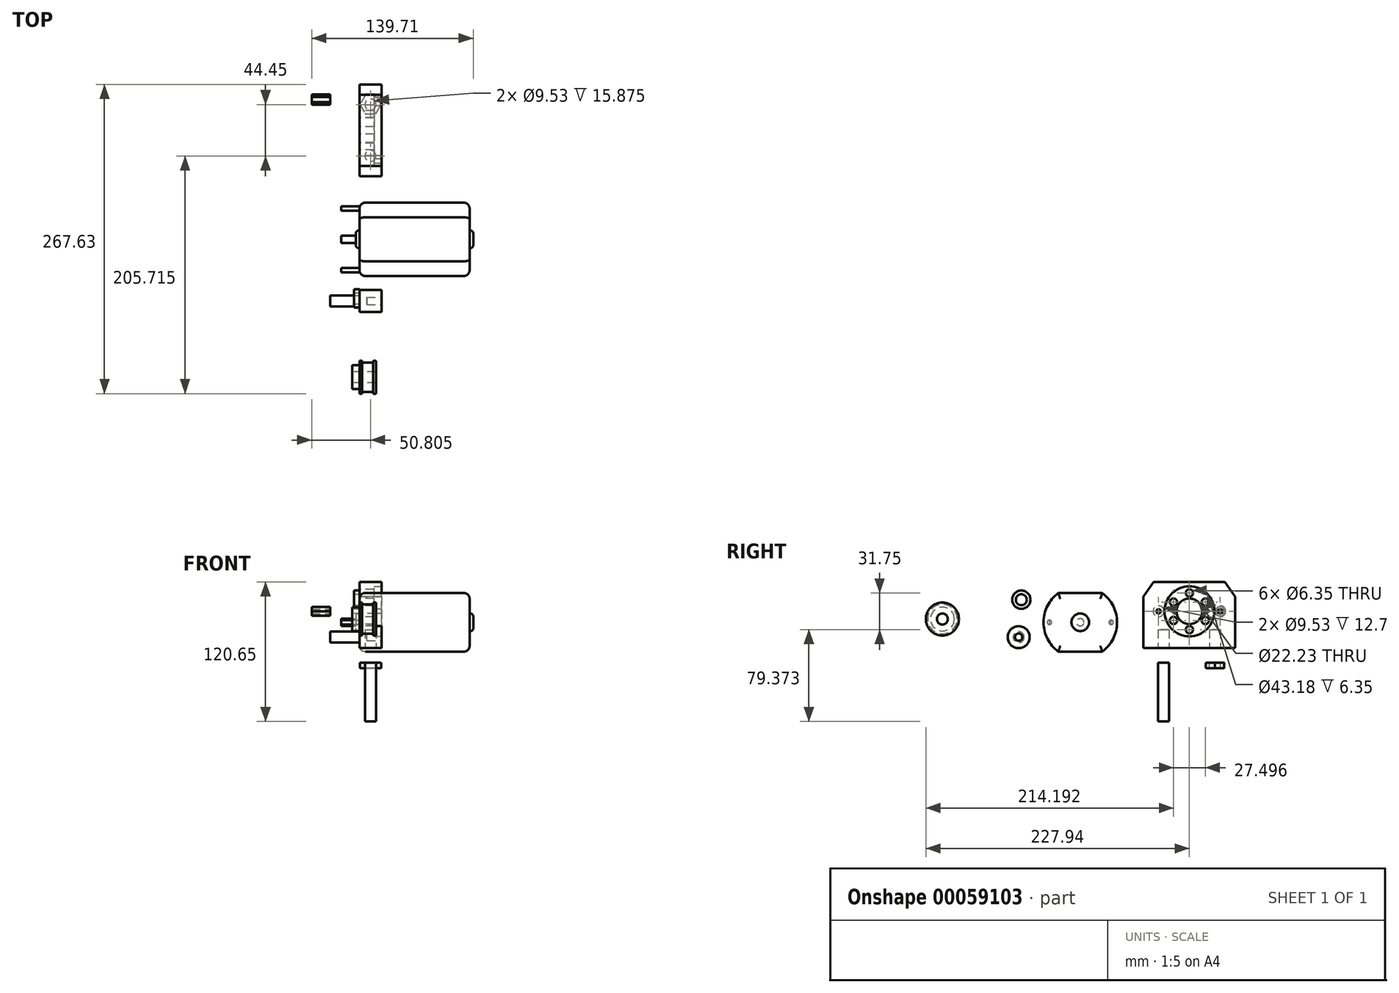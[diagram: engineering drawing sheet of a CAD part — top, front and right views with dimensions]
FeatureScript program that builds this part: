
annotation { "Feature Type Name" : "Feature", "Feature Type Description" : "" }
export const myFeature = defineFeature(function(context is Context, id is Id, definition is map)
    precondition{}
    {
        {
            var Q0;
            Q0=qCreatedBy(makeId("Right.planeOp"),FACE);
            var sketch = newSketch(context, id + "F0", { "sketchPlane" : qUnion([Q0])});
            skLineSegment(sketch, "E0.bottom", {"start": v(-22.45, 10.6) * mm, "end": v(15.65, 10.6) * mm});
            skLineSegment(sketch, "E0.top", {"start": v(-22.45, -40.2) * mm, "end": v(15.65, -40.2) * mm});
            skLineSegment(sketch, "E1", {"start": v(-22.45, 10.6) * mm, "end": v(-22.45, -40.2) * mm, "construction": true});
            skLineSegment(sketch, "E2", {"start": v(15.65, 10.6) * mm, "end": v(15.65, -40.2) * mm, "construction": true});
            skArc(sketch, "E3", {"start": v(-22.45, 10.6) * mm, "mid": v(-35.15, -14.8) * mm, "end": v(-22.45, -40.2) * mm});
            skArc(sketch, "E4", {"start": v(15.65, -40.2) * mm, "mid": v(28.35, -14.8) * mm, "end": v(15.65, 10.6) * mm});
            skSolve(sketch);
        }
        {
            var Q0;
            Q0=makeQuery(id+"F0.imprint","IMPRINT",FACE,{"disambiguationData":[TD([[makeQuery(id+"F0.imprint","IMPRINT",EDGE,{"derivedFrom":sQuery(id+"F0.wireOp",EDGE,"E0.bottom")}),-1.0]])]});
            extrude(context, id + "F1", {"entities" : qUnion([Q0]), "depth" : 95.25 * mm});
        }
        {
            var Q0;
            Q0=makeQuery(id+"F1.opExtrude","CAP_EDGE",EDGE,{"disambiguationData":[OSD([sQuery(id+"F0.wireOp",EDGE,"E3")])],"isStart":false});
            var Q1;
            Q1=makeQuery(id+"F1.opExtrude","CAP_EDGE",EDGE,{"disambiguationData":[OSD([sQuery(id+"F0.wireOp",EDGE,"E4")])],"isStart":false});
            var Q2;
            Q2=makeQuery(id+"F1.opExtrude","CAP_EDGE",EDGE,{"disambiguationData":[OSD([sQuery(id+"F0.wireOp",EDGE,"E0.bottom")])],"isStart":false});
            var Q3;
            Q3=makeQuery(id+"F1.opExtrude","CAP_EDGE",EDGE,{"disambiguationData":[OSD([sQuery(id+"F0.wireOp",EDGE,"E0.top")])],"isStart":false});
            fillet(context, id + "F2", {"entities" : qUnion([Q0, Q1, Q2, Q3]), "radius" : 5.08 * mm, "tangentPropagation" : true, "allowEdgeOverflow" : false});
        }
        {
            var Q0;
            Q0=makeQuery(id+"F1.opExtrude","CAP_EDGE",EDGE,{"disambiguationData":[OSD([sQuery(id+"F0.wireOp",EDGE,"E0.bottom")])],"isStart":true});
            var Q1;
            Q1=makeQuery(id+"F1.opExtrude","CAP_EDGE",EDGE,{"disambiguationData":[OSD([sQuery(id+"F0.wireOp",EDGE,"E0.top")])],"isStart":true});
            var Q2;
            Q2=makeQuery(id+"F1.opExtrude","CAP_EDGE",EDGE,{"disambiguationData":[OSD([sQuery(id+"F0.wireOp",EDGE,"E3")])],"isStart":true});
            var Q3;
            Q3=makeQuery(id+"F1.opExtrude","CAP_EDGE",EDGE,{"disambiguationData":[OSD([sQuery(id+"F0.wireOp",EDGE,"E4")])],"isStart":true});
            fillet(context, id + "F3", {"entities" : qUnion([Q0, Q1, Q2, Q3]), "radius" : 5.08 * mm, "tangentPropagation" : true, "allowEdgeOverflow" : false});
        }
        {
            var Q0;
            Q0=makeQuery(id+"F1.opExtrude","CAP_FACE",FACE,{"disambiguationData":[OSD([sQuery(id+"F0.wireOp",EDGE,"E0.bottom"),sQuery(id+"F0.wireOp",EDGE,"E0.top"),sQuery(id+"F0.wireOp",EDGE,"E3"),sQuery(id+"F0.wireOp",EDGE,"E4")])],"isStart":true});
            var sketch = newSketch(context, id + "F4", { "sketchPlane" : qUnion([Q0])});
            skLineSegment(sketch, "E5", {"start": v(-23.27, -14.8) * mm, "end": v(30.07, -14.8) * mm, "construction": true});
            skLineSegment(sketch, "E6", {"start": v(3.4, 5.53) * mm, "end": v(3.4, -35.11) * mm, "construction": true});
            skCircle(sketch, "E7", {"center": v(3.4, -14.8) * mm, "radius": 7.62 * mm});
            skSolve(sketch);
        }
        {
            var Q0;
            Q0=makeQuery(id+"F4.imprint","IMPRINT",FACE,{"disambiguationData":[TD([[makeQuery(id+"F4.imprint","IMPRINT",EDGE,{"derivedFrom":sQuery(id+"F4.wireOp",EDGE,"E7")}),1.0]])]});
            extrude(context, id + "F5", {"entities" : qUnion([Q0]), "operationType" : NewBodyOperationType.ADD, "depth" : 3.17 * mm});
        }
        {
            var Q0;
            Q0=makeQuery(id+"F5.opExtrude","CAP_FACE",FACE,{"disambiguationData":[OSD([sQuery(id+"F4.wireOp",EDGE,"E7")])],"isStart":false});
            var sketch = newSketch(context, id + "F6", { "sketchPlane" : qUnion([Q0])});
            skCircle(sketch, "E8", {"center": v(3.4, -14.8) * mm, "radius": 3.18 * mm});
            skSolve(sketch);
        }
        {
            var Q0;
            Q0=makeQuery(id+"F6.imprint","IMPRINT",FACE,{"disambiguationData":[TD([[makeQuery(id+"F6.imprint","IMPRINT",EDGE,{"derivedFrom":sQuery(id+"F6.wireOp",EDGE,"E8")}),1.0]])]});
            extrude(context, id + "F7", {"entities" : qUnion([Q0]), "operationType" : NewBodyOperationType.ADD, "depth" : 12.7 * mm});
        }
        {
            var Q0;
            Q0=makeQuery(id+"F5.opExtrude","CAP_EDGE",EDGE,{"disambiguationData":[OSD([sQuery(id+"F4.wireOp",EDGE,"E7")])],"isStart":false});
            fillet(context, id + "F8", {"entities" : qUnion([Q0]), "radius" : 2.54 * mm, "tangentPropagation" : true, "allowEdgeOverflow" : false});
        }
        {
            var Q0;
            Q0=makeQuery(id+"F1.opExtrude","CAP_FACE",FACE,{"disambiguationData":[OSD([sQuery(id+"F0.wireOp",EDGE,"E0.bottom"),sQuery(id+"F0.wireOp",EDGE,"E0.top"),sQuery(id+"F0.wireOp",EDGE,"E3"),sQuery(id+"F0.wireOp",EDGE,"E4")])],"isStart":false});
            var sketch = newSketch(context, id + "F9", { "sketchPlane" : qUnion([Q0])});
            skLineSegment(sketch, "E9", {"start": v(-30.07, -14.8) * mm, "end": v(23.27, -14.8) * mm, "construction": true});
            skLineSegment(sketch, "E10", {"start": v(-3.4, 5.53) * mm, "end": v(-3.4, -35.11) * mm, "construction": true});
            skCircle(sketch, "E11", {"center": v(-3.4, -14.8) * mm, "radius": 7.62 * mm});
            skSolve(sketch);
        }
        {
            var Q0;
            Q0=makeQuery(id+"F9.imprint","IMPRINT",FACE,{"disambiguationData":[TD([[makeQuery(id+"F9.imprint","IMPRINT",EDGE,{"derivedFrom":sQuery(id+"F9.wireOp",EDGE,"E11")}),1.0]])]});
            extrude(context, id + "F10", {"entities" : qUnion([Q0]), "operationType" : NewBodyOperationType.ADD, "depth" : 3.17 * mm});
        }
        {
            var Q0;
            Q0=makeQuery(id+"F10.opExtrude","CAP_EDGE",EDGE,{"disambiguationData":[OSD([sQuery(id+"F9.wireOp",EDGE,"E11")])],"isStart":false});
            fillet(context, id + "F11", {"entities" : qUnion([Q0]), "radius" : 2.54 * mm, "tangentPropagation" : true, "allowEdgeOverflow" : false});
        }
        {
            var Q0;
            Q0=makeQuery(id+"F1.opExtrude","CAP_FACE",FACE,{"disambiguationData":[OSD([sQuery(id+"F0.wireOp",EDGE,"E0.bottom"),sQuery(id+"F0.wireOp",EDGE,"E0.top"),sQuery(id+"F0.wireOp",EDGE,"E3"),sQuery(id+"F0.wireOp",EDGE,"E4")])],"isStart":true});
            var sketch = newSketch(context, id + "F12", { "sketchPlane" : qUnion([Q0])});
            skLineSegment(sketch, "E12", {"start": v(-23.27, -14.8) * mm, "end": v(30.07, -14.8) * mm, "construction": true});
            skCircle(sketch, "E13", {"center": v(-23.27, -14.8) * mm, "radius": 1.9 * mm});
            skCircle(sketch, "E14", {"center": v(30.07, -14.8) * mm, "radius": 1.9 * mm});
            skSolve(sketch);
        }
        {
            var Q0;
            {var subQ0=sQuery(id+"F12.wireOp",EDGE,"E13");var subQ1=sQuery(id+"F0.wireOp",EDGE,"E4");var subQ2=makeQuery(id+"F3.opFillet","BLEND_EDGE",EDGE,{"blendedFrom":[makeQuery(id+"F1.opExtrude","CAP_EDGE",EDGE,{"disambiguationData":[OSD([subQ1])],"isStart":true}),makeQuery(id+"F1.opExtrude","CAP_FACE",FACE,{"disambiguationData":[OSD([sQuery(id+"F0.wireOp",EDGE,"E0.bottom"),sQuery(id+"F0.wireOp",EDGE,"E0.top"),sQuery(id+"F0.wireOp",EDGE,"E3"),subQ1])],"isStart":true})],"blendedInto":[makeQuery(id+"F1.opExtrude","CAP_FACE",FACE,{"disambiguationData":[OSD([sQuery(id+"F0.wireOp",EDGE,"E0.bottom"),sQuery(id+"F0.wireOp",EDGE,"E0.top"),sQuery(id+"F0.wireOp",EDGE,"E3"),subQ1])],"isStart":true})]});var subQ3=makeQuery(id+"F12.imprint","INTERSECT",VERTEX,{"disambiguationData":[OD(0.0)],"derivedFrom":[subQ2,subQ0]});Q0=makeQuery(id+"F12.imprint","IMPRINT",FACE,{"disambiguationData":[TD([[makeQuery(id+"F12.imprint","IMPRINT",EDGE,{"disambiguationData":[TD([[subQ3,1.0]])],"derivedFrom":subQ0}),1.0]])]});}
            var Q1;
            {var subQ0=sQuery(id+"F12.wireOp",EDGE,"E13");var subQ1=sQuery(id+"F0.wireOp",EDGE,"E4");var subQ2=makeQuery(id+"F3.opFillet","BLEND_EDGE",EDGE,{"blendedFrom":[makeQuery(id+"F1.opExtrude","CAP_EDGE",EDGE,{"disambiguationData":[OSD([subQ1])],"isStart":true}),makeQuery(id+"F1.opExtrude","CAP_FACE",FACE,{"disambiguationData":[OSD([sQuery(id+"F0.wireOp",EDGE,"E0.bottom"),sQuery(id+"F0.wireOp",EDGE,"E0.top"),sQuery(id+"F0.wireOp",EDGE,"E3"),subQ1])],"isStart":true})],"blendedInto":[makeQuery(id+"F1.opExtrude","CAP_FACE",FACE,{"disambiguationData":[OSD([sQuery(id+"F0.wireOp",EDGE,"E0.bottom"),sQuery(id+"F0.wireOp",EDGE,"E0.top"),sQuery(id+"F0.wireOp",EDGE,"E3"),subQ1])],"isStart":true})]});var subQ3=makeQuery(id+"F12.imprint","INTERSECT",VERTEX,{"disambiguationData":[OD(0.0)],"derivedFrom":[subQ2,subQ0]});Q1=makeQuery(id+"F12.imprint","IMPRINT",FACE,{"disambiguationData":[TD([[makeQuery(id+"F12.imprint","IMPRINT",EDGE,{"disambiguationData":[TD([[subQ3,-1.0]])],"derivedFrom":subQ0}),1.0]])]});}
            var Q2;
            {var subQ0=sQuery(id+"F12.wireOp",EDGE,"E14");var subQ1=sQuery(id+"F0.wireOp",EDGE,"E3");var subQ2=makeQuery(id+"F3.opFillet","BLEND_EDGE",EDGE,{"blendedFrom":[makeQuery(id+"F1.opExtrude","CAP_EDGE",EDGE,{"disambiguationData":[OSD([subQ1])],"isStart":true}),makeQuery(id+"F1.opExtrude","CAP_FACE",FACE,{"disambiguationData":[OSD([sQuery(id+"F0.wireOp",EDGE,"E0.bottom"),sQuery(id+"F0.wireOp",EDGE,"E0.top"),subQ1,sQuery(id+"F0.wireOp",EDGE,"E4")])],"isStart":true})],"blendedInto":[makeQuery(id+"F1.opExtrude","CAP_FACE",FACE,{"disambiguationData":[OSD([sQuery(id+"F0.wireOp",EDGE,"E0.bottom"),sQuery(id+"F0.wireOp",EDGE,"E0.top"),subQ1,sQuery(id+"F0.wireOp",EDGE,"E4")])],"isStart":true})]});var subQ3=makeQuery(id+"F12.imprint","INTERSECT",VERTEX,{"disambiguationData":[OD(0.0)],"derivedFrom":[subQ2,subQ0]});Q2=makeQuery(id+"F12.imprint","IMPRINT",FACE,{"disambiguationData":[TD([[makeQuery(id+"F12.imprint","IMPRINT",EDGE,{"disambiguationData":[TD([[subQ3,-1.0]])],"derivedFrom":subQ0}),1.0]])]});}
            var Q3;
            {var subQ0=sQuery(id+"F12.wireOp",EDGE,"E14");var subQ1=sQuery(id+"F0.wireOp",EDGE,"E3");var subQ2=makeQuery(id+"F3.opFillet","BLEND_EDGE",EDGE,{"blendedFrom":[makeQuery(id+"F1.opExtrude","CAP_EDGE",EDGE,{"disambiguationData":[OSD([subQ1])],"isStart":true}),makeQuery(id+"F1.opExtrude","CAP_FACE",FACE,{"disambiguationData":[OSD([sQuery(id+"F0.wireOp",EDGE,"E0.bottom"),sQuery(id+"F0.wireOp",EDGE,"E0.top"),subQ1,sQuery(id+"F0.wireOp",EDGE,"E4")])],"isStart":true})],"blendedInto":[makeQuery(id+"F1.opExtrude","CAP_FACE",FACE,{"disambiguationData":[OSD([sQuery(id+"F0.wireOp",EDGE,"E0.bottom"),sQuery(id+"F0.wireOp",EDGE,"E0.top"),subQ1,sQuery(id+"F0.wireOp",EDGE,"E4")])],"isStart":true})]});var subQ3=makeQuery(id+"F12.imprint","INTERSECT",VERTEX,{"disambiguationData":[OD(0.0)],"derivedFrom":[subQ2,subQ0]});Q3=makeQuery(id+"F12.imprint","IMPRINT",FACE,{"disambiguationData":[TD([[makeQuery(id+"F12.imprint","IMPRINT",EDGE,{"disambiguationData":[TD([[subQ3,1.0]])],"derivedFrom":subQ0}),1.0]])]});}
            extrude(context, id + "F13", {"entities" : qUnion([Q0, Q1, Q2, Q3]), "operationType" : NewBodyOperationType.ADD, "depth" : 15.88 * mm});
        }
        {
            var Q0;
            Q0=qCreatedBy(makeId("Right.planeOp"),FACE);
            var sketch = newSketch(context, id + "F14", { "sketchPlane" : qUnion([Q0])});
            skLineSegment(sketch, "E15.bottom", {"start": v(130.66, 20.15) * mm, "end": v(51.28, 20.15) * mm});
            skLineSegment(sketch, "E15.top", {"start": v(130.66, -37) * mm, "end": v(51.28, -37) * mm});
            skLineSegment(sketch, "E15.left", {"start": v(130.66, 20.15) * mm, "end": v(130.66, -37) * mm});
            skLineSegment(sketch, "E15.right", {"start": v(51.28, 20.15) * mm, "end": v(51.28, -37) * mm});
            skLineSegment(sketch, "E16", {"start": v(117.64, 20.15) * mm, "end": v(117.64, -37) * mm, "construction": true});
            skLineSegment(sketch, "E17", {"start": v(64.3, 20.15) * mm, "end": v(64.3, -37) * mm, "construction": true});
            skLineSegment(sketch, "E18", {"start": v(130.66, -5.25) * mm, "end": v(51.28, -5.25) * mm, "construction": true});
            skCircle(sketch, "E19", {"center": v(117.64, -5.25) * mm, "radius": 1.9 * mm});
            skCircle(sketch, "E20", {"center": v(64.3, -5.25) * mm, "radius": 1.9 * mm});
            skLineSegment(sketch, "E21", {"start": v(90.97, 20.15) * mm, "end": v(90.97, -37) * mm, "construction": true});
            skSolve(sketch);
        }
        {
            var Q0;
            Q0=makeQuery(id+"F14.imprint","IMPRINT",FACE,{"disambiguationData":[TD([[makeQuery(id+"F14.imprint","IMPRINT",EDGE,{"derivedFrom":sQuery(id+"F14.wireOp",EDGE,"E15.bottom")}),1.0]])]});
            extrude(context, id + "F15", {"entities" : qUnion([Q0]), "depth" : 19.05 * mm});
        }
        {
            var Q0;
            Q0=makeQuery(id+"F15.opExtrude","CAP_FACE",FACE,{"disambiguationData":[OSD([sQuery(id+"F14.wireOp",EDGE,"E15.bottom"),sQuery(id+"F14.wireOp",EDGE,"E15.top"),sQuery(id+"F14.wireOp",EDGE,"E15.left"),sQuery(id+"F14.wireOp",EDGE,"E15.right"),sQuery(id+"F14.wireOp",EDGE,"E19"),sQuery(id+"F14.wireOp",EDGE,"E20")])],"isStart":true});
            var sketch = newSketch(context, id + "F16", { "sketchPlane" : qUnion([Q0])});
            skCircle(sketch, "E22", {"center": v(-117.64, -5.25) * mm, "radius": 4.76 * mm});
            skCircle(sketch, "E23", {"center": v(-64.3, -5.25) * mm, "radius": 4.76 * mm});
            skSolve(sketch);
        }
        {
            var Q0;
            Q0=makeQuery(id+"F16.imprint","IMPRINT",FACE,{"disambiguationData":[TD([[makeQuery(id+"F16.imprint","IMPRINT",EDGE,{"derivedFrom":sQuery(id+"F16.wireOp",EDGE,"E22")}),1.0]])]});
            var Q1;
            Q1=makeQuery(id+"F16.imprint","IMPRINT",FACE,{"disambiguationData":[TD([[makeQuery(id+"F16.imprint","IMPRINT",EDGE,{"derivedFrom":sQuery(id+"F16.wireOp",EDGE,"E23")}),1.0]])]});
            extrude(context, id + "F17", {"entities" : qUnion([Q0, Q1]), "operationType" : NewBodyOperationType.REMOVE, "oppositeDirection" : true, "depth" : 12.7 * mm});
        }
        {
            var Q0;
            Q0=makeQuery(id+"F15.opExtrude","CAP_FACE",FACE,{"disambiguationData":[OSD([sQuery(id+"F14.wireOp",EDGE,"E15.bottom"),sQuery(id+"F14.wireOp",EDGE,"E15.top"),sQuery(id+"F14.wireOp",EDGE,"E15.left"),sQuery(id+"F14.wireOp",EDGE,"E15.right"),sQuery(id+"F14.wireOp",EDGE,"E19"),sQuery(id+"F14.wireOp",EDGE,"E20")])],"isStart":true});
            var sketch = newSketch(context, id + "F18", { "sketchPlane" : qUnion([Q0])});
            skLineSegment(sketch, "E24", {"start": v(-90.97, 20.15) * mm, "end": v(-90.97, -37) * mm, "construction": true});
            skLineSegment(sketch, "E25", {"start": v(-117.64, -5.25) * mm, "end": v(-64.3, -5.25) * mm, "construction": true});
            skCircle(sketch, "E26", {"center": v(-90.97, -5.25) * mm, "radius": 11.11 * mm});
            skPoint(sketch, "E26.centerSnap1", {"position": v(-90.97, -5.25) * mm});
            skSolve(sketch);
        }
        {
            var Q0;
            Q0=makeQuery(id+"F18.imprint","IMPRINT",FACE,{"disambiguationData":[TD([[makeQuery(id+"F18.imprint","IMPRINT",EDGE,{"derivedFrom":sQuery(id+"F18.wireOp",EDGE,"E26")}),1.0]])]});
            extrude(context, id + "F19", {"entities" : qUnion([Q0]), "operationType" : NewBodyOperationType.REMOVE, "endBound" : BoundingType.THROUGH_ALL, "oppositeDirection" : true, "depth" : 25.4 * mm});
        }
        {
            var Q0;
            Q0=makeQuery(id+"F15.opExtrude","SWEPT_EDGE",EDGE,{"disambiguationData":[OSD([sQuery(id+"F14.wireOp",EDGE,"E15.bottom"),sQuery(id+"F14.wireOp",EDGE,"E15.left")])]});
            var Q1;
            Q1=makeQuery(id+"F15.opExtrude","SWEPT_EDGE",EDGE,{"disambiguationData":[OSD([sQuery(id+"F14.wireOp",EDGE,"E15.bottom"),sQuery(id+"F14.wireOp",EDGE,"E15.right")])]});
            chamfer(context, id + "F20", {"entities" : qUnion([Q0, Q1]), "chamferType" : ChamferType.TWO_OFFSETS, "width1" : 8.9 * mm, "oppositeDirection" : false, "width2" : 12.7 * mm, "tangentPropagation" : true});
        }
        {
            var Q0;
            Q0=makeQuery(id+"F15.opExtrude","SWEPT_FACE",FACE,{"disambiguationData":[OSD([sQuery(id+"F14.wireOp",EDGE,"E15.top")])]});
            var sketch = newSketch(context, id + "F21", { "sketchPlane" : qUnion([Q0])});
            skLineSegment(sketch, "E27", {"start": v(9.53, -51.28) * mm, "end": v(9.53, -130.66) * mm, "construction": true});
            skLineSegment(sketch, "E28", {"start": v(0, -68.74) * mm, "end": v(19.05, -68.74) * mm, "construction": true});
            skLineSegment(sketch, "E29", {"start": v(0, -113.2) * mm, "end": v(19.05, -113.2) * mm, "construction": true});
            skCircle(sketch, "E30", {"center": v(9.53, -68.74) * mm, "radius": 4.76 * mm});
            skCircle(sketch, "E31", {"center": v(9.53, -113.2) * mm, "radius": 4.76 * mm});
            skLineSegment(sketch, "E32.0", {"start": v(19.05, -51.28) * mm, "end": v(0, -51.28) * mm, "construction": true});
            skLineSegment(sketch, "E33.0", {"start": v(19.05, -130.66) * mm, "end": v(0, -130.66) * mm, "construction": true});
            skLineSegment(sketch, "E34", {"start": v(0, -90.97) * mm, "end": v(19.05, -90.97) * mm, "construction": true});
            skSolve(sketch);
        }
        {
            var Q0;
            Q0=makeQuery(id+"F21.imprint","IMPRINT",FACE,{"disambiguationData":[TD([[makeQuery(id+"F21.imprint","IMPRINT",EDGE,{"derivedFrom":sQuery(id+"F21.wireOp",EDGE,"E30")}),1.0]])]});
            var Q1;
            Q1=makeQuery(id+"F21.imprint","IMPRINT",FACE,{"disambiguationData":[TD([[makeQuery(id+"F21.imprint","IMPRINT",EDGE,{"derivedFrom":sQuery(id+"F21.wireOp",EDGE,"E31")}),1.0]])]});
            extrude(context, id + "F22", {"entities" : qUnion([Q0, Q1]), "operationType" : NewBodyOperationType.REMOVE, "oppositeDirection" : true, "depth" : 15.88 * mm});
        }
        {
            var Q0;
            Q0=makeQuery(id+"F15.opExtrude","CAP_FACE",FACE,{"disambiguationData":[OSD([sQuery(id+"F14.wireOp",EDGE,"E15.bottom"),sQuery(id+"F14.wireOp",EDGE,"E15.top"),sQuery(id+"F14.wireOp",EDGE,"E15.left"),sQuery(id+"F14.wireOp",EDGE,"E15.right"),sQuery(id+"F14.wireOp",EDGE,"E19"),sQuery(id+"F14.wireOp",EDGE,"E20")])],"isStart":true});
            var sketch = newSketch(context, id + "F23", { "sketchPlane" : qUnion([Q0])});
            skCircle(sketch, "E35", {"center": v(-90.97, 10.62) * mm, "radius": 3.18 * mm});
            skCircle(sketch, "E36.1.0", {"center": v(-104.72, 2.69) * mm, "radius": 3.18 * mm});
            skCircle(sketch, "E36.2.0", {"center": v(-104.72, -13.19) * mm, "radius": 3.18 * mm});
            skCircle(sketch, "E36.3.0", {"center": v(-90.97, -21.13) * mm, "radius": 3.18 * mm});
            skCircle(sketch, "E36.4.0", {"center": v(-77.22, -13.19) * mm, "radius": 3.18 * mm});
            skCircle(sketch, "E36.5.0", {"center": v(-77.22, 2.69) * mm, "radius": 3.18 * mm});
            skPoint(sketch, "E36.center", {"position": v(-90.97, -5.25) * mm});
            skPoint(sketch, "E37.orphan", {"position": v(-90.97, 20.15) * mm});
            skLineSegment(sketch, "E38", {"start": v(-90.97, 20.15) * mm, "end": v(-90.97, -37) * mm, "construction": true});
            skLineSegment(sketch, "E39", {"start": v(-90.97, -37) * mm, "end": v(-92.08, -36.2) * mm, "construction": true});
            skSolve(sketch);
        }
        {
            var Q0;
            Q0=makeQuery(id+"F23.imprint","IMPRINT",FACE,{"disambiguationData":[TD([[makeQuery(id+"F23.imprint","IMPRINT",EDGE,{"derivedFrom":sQuery(id+"F23.wireOp",EDGE,"E35")}),1.0]])]});
            var Q1;
            Q1=makeQuery(id+"F23.imprint","IMPRINT",FACE,{"disambiguationData":[TD([[makeQuery(id+"F23.imprint","IMPRINT",EDGE,{"derivedFrom":sQuery(id+"F23.wireOp",EDGE,"E36.5.0")}),1.0]])]});
            var Q2;
            Q2=makeQuery(id+"F23.imprint","IMPRINT",FACE,{"disambiguationData":[TD([[makeQuery(id+"F23.imprint","IMPRINT",EDGE,{"derivedFrom":sQuery(id+"F23.wireOp",EDGE,"E36.4.0")}),1.0]])]});
            var Q3;
            Q3=makeQuery(id+"F23.imprint","IMPRINT",FACE,{"disambiguationData":[TD([[makeQuery(id+"F23.imprint","IMPRINT",EDGE,{"derivedFrom":sQuery(id+"F23.wireOp",EDGE,"E36.3.0")}),1.0]])]});
            var Q4;
            Q4=makeQuery(id+"F23.imprint","IMPRINT",FACE,{"disambiguationData":[TD([[makeQuery(id+"F23.imprint","IMPRINT",EDGE,{"derivedFrom":sQuery(id+"F23.wireOp",EDGE,"E36.2.0")}),1.0]])]});
            var Q5;
            Q5=makeQuery(id+"F23.imprint","IMPRINT",FACE,{"disambiguationData":[TD([[makeQuery(id+"F23.imprint","IMPRINT",EDGE,{"derivedFrom":sQuery(id+"F23.wireOp",EDGE,"E36.1.0")}),1.0]])]});
            extrude(context, id + "F24", {"entities" : qUnion([Q0, Q1, Q2, Q3, Q4, Q5]), "operationType" : NewBodyOperationType.REMOVE, "endBound" : BoundingType.THROUGH_ALL, "oppositeDirection" : true, "depth" : 25.4 * mm});
        }
        {
            var Q0;
            Q0=makeQuery(id+"F15.opExtrude","CAP_FACE",FACE,{"disambiguationData":[OSD([sQuery(id+"F14.wireOp",EDGE,"E15.bottom"),sQuery(id+"F14.wireOp",EDGE,"E15.top"),sQuery(id+"F14.wireOp",EDGE,"E15.left"),sQuery(id+"F14.wireOp",EDGE,"E15.right"),sQuery(id+"F14.wireOp",EDGE,"E19"),sQuery(id+"F14.wireOp",EDGE,"E20")])],"isStart":false});
            var sketch = newSketch(context, id + "F25", { "sketchPlane" : qUnion([Q0])});
            skCircle(sketch, "E40.0", {"center": v(90.97, -5.25) * mm, "radius": 11.11 * mm});
            skCircle(sketch, "E41", {"center": v(90.97, -5.25) * mm, "radius": 21.59 * mm});
            skSolve(sketch);
        }
        {
            var Q0;
            Q0=makeQuery(id+"F25.imprint","IMPRINT",FACE,{"disambiguationData":[TD([[makeQuery(id+"F25.imprint","IMPRINT",EDGE,{"derivedFrom":sQuery(id+"F25.wireOp",EDGE,"E40.0")}),-1.0]])]});
            extrude(context, id + "F26", {"entities" : qUnion([Q0]), "operationType" : NewBodyOperationType.REMOVE, "oppositeDirection" : true, "depth" : 6.35 * mm});
        }
        {
            var Q0;
            Q0=qCreatedBy(makeId("Right.planeOp"),FACE);
            var sketch = newSketch(context, id + "F27", { "sketchPlane" : qUnion([Q0])});
            skCircle(sketch, "E42", {"center": v(-56.7, -27.63) * mm, "radius": 9.53 * mm});
            skSolve(sketch);
        }
        {
            var Q0;
            Q0=makeQuery(id+"F27.imprint","IMPRINT",FACE,{"disambiguationData":[TD([[makeQuery(id+"F27.imprint","IMPRINT",EDGE,{"derivedFrom":sQuery(id+"F27.wireOp",EDGE,"E42")}),1.0]])]});
            extrude(context, id + "F28", {"entities" : qUnion([Q0]), "depth" : 19.05 * mm});
        }
        {
            var Q0;
            Q0=makeQuery(id+"F28.opExtrude","CAP_FACE",FACE,{"disambiguationData":[OSD([sQuery(id+"F27.wireOp",EDGE,"E42")])],"isStart":true});
            var sketch = newSketch(context, id + "F29", { "sketchPlane" : qUnion([Q0])});
            skCircle(sketch, "E43", {"center": v(56.7, -27.63) * mm, "radius": 4.76 * mm});
            skSolve(sketch);
        }
        {
            var Q0;
            Q0=makeQuery(id+"F29.imprint","IMPRINT",FACE,{"disambiguationData":[TD([[makeQuery(id+"F29.imprint","IMPRINT",EDGE,{"derivedFrom":sQuery(id+"F29.wireOp",EDGE,"E43")}),1.0]])]});
            extrude(context, id + "F30", {"entities" : qUnion([Q0]), "operationType" : NewBodyOperationType.ADD, "depth" : 25.4 * mm});
        }
        {
            var Q0;
            Q0=makeQuery(id+"F28.opExtrude","CAP_FACE",FACE,{"disambiguationData":[OSD([sQuery(id+"F27.wireOp",EDGE,"E42")])],"isStart":false});
            var sketch = newSketch(context, id + "F31", { "sketchPlane" : qUnion([Q0])});
            skCircle(sketch, "E44", {"center": v(-56.7, -27.63) * mm, "radius": 3.17 * mm});
            skSolve(sketch);
        }
        {
            var Q0;
            Q0=makeQuery(id+"F31.imprint","IMPRINT",FACE,{"disambiguationData":[TD([[makeQuery(id+"F31.imprint","IMPRINT",EDGE,{"derivedFrom":sQuery(id+"F31.wireOp",EDGE,"E44")}),1.0]])]});
            extrude(context, id + "F32", {"entities" : qUnion([Q0]), "operationType" : NewBodyOperationType.REMOVE, "oppositeDirection" : true, "depth" : 12.7 * mm});
        }
        {
            var Q0;
            Q0=qCreatedBy(makeId("Right.planeOp"),FACE);
            var sketch = newSketch(context, id + "F33", { "sketchPlane" : qUnion([Q0])});
            skCircle(sketch, "E45", {"center": v(-122.68, -11.96) * mm, "radius": 14.29 * mm});
            skCircle(sketch, "E46", {"center": v(-122.68, -11.96) * mm, "radius": 4.76 * mm});
            skSolve(sketch);
        }
        {
            var Q0;
            Q0=makeQuery(id+"F33.imprint","IMPRINT",FACE,{"disambiguationData":[TD([[makeQuery(id+"F33.imprint","IMPRINT",EDGE,{"derivedFrom":sQuery(id+"F33.wireOp",EDGE,"E45")}),1.0]])]});
            extrude(context, id + "F34", {"entities" : qUnion([Q0]), "depth" : 2.4 * mm});
        }
        {
            var Q0;
            Q0=makeQuery(id+"F34.opExtrude","CAP_FACE",FACE,{"disambiguationData":[OSD([sQuery(id+"F33.wireOp",EDGE,"E45"),sQuery(id+"F33.wireOp",EDGE,"E46")])],"isStart":true});
            var sketch = newSketch(context, id + "F35", { "sketchPlane" : qUnion([Q0])});
            skCircle(sketch, "E47", {"center": v(122.68, -11.96) * mm, "radius": 10.31 * mm});
            skSolve(sketch);
        }
        {
            var Q0;
            Q0=makeQuery(id+"F35.imprint","IMPRINT",FACE,{"disambiguationData":[TD([[makeQuery(id+"F35.imprint","IMPRINT",EDGE,{"derivedFrom":sQuery(id+"F35.wireOp",EDGE,"E47")}),1.0]])]});
            extrude(context, id + "F36", {"entities" : qUnion([Q0]), "operationType" : NewBodyOperationType.ADD, "depth" : 6.35 * mm});
        }
        {
            var Q0;
            Q0=makeQuery(id+"F34.opExtrude","CAP_FACE",FACE,{"disambiguationData":[OSD([sQuery(id+"F33.wireOp",EDGE,"E45"),sQuery(id+"F33.wireOp",EDGE,"E46")])],"isStart":false});
            var sketch = newSketch(context, id + "F37", { "sketchPlane" : qUnion([Q0])});
            skCircle(sketch, "E48", {"center": v(-122.68, -11.96) * mm, "radius": 12.7 * mm});
            skCircle(sketch, "E49", {"center": v(-122.68, -11.96) * mm, "radius": 4.76 * mm});
            skSolve(sketch);
        }
        {
            var Q0;
            Q0=makeQuery(id+"F37.imprint","IMPRINT",FACE,{"disambiguationData":[TD([[makeQuery(id+"F37.imprint","IMPRINT",EDGE,{"derivedFrom":sQuery(id+"F37.wireOp",EDGE,"E48")}),1.0]])]});
            extrude(context, id + "F38", {"entities" : qUnion([Q0]), "operationType" : NewBodyOperationType.ADD, "depth" : 11.9 * mm});
        }
        {
            var Q0;
            Q0=makeQuery(id+"F38.opExtrude","CAP_FACE",FACE,{"disambiguationData":[OSD([sQuery(id+"F37.wireOp",EDGE,"E48"),sQuery(id+"F37.wireOp",EDGE,"E49")])],"isStart":false});
            var sketch = newSketch(context, id + "F39", { "sketchPlane" : qUnion([Q0])});
            skCircle(sketch, "E50", {"center": v(-122.68, -11.96) * mm, "radius": 4.76 * mm});
            skCircle(sketch, "E51", {"center": v(-122.68, -11.96) * mm, "radius": 14.29 * mm});
            skSolve(sketch);
        }
        {
            var Q0;
            Q0=makeQuery(id+"F39.imprint","IMPRINT",FACE,{"disambiguationData":[TD([[makeQuery(id+"F39.imprint","IMPRINT",EDGE,{"derivedFrom":sQuery(id+"F39.wireOp",EDGE,"E51")}),1.0]])]});
            extrude(context, id + "F40", {"entities" : qUnion([Q0]), "operationType" : NewBodyOperationType.ADD, "oppositeDirection" : true, "depth" : 2.4 * mm});
        }
        {
            var Q0;
            Q0=qCreatedBy(makeId("Right.planeOp"),FACE);
            var sketch = newSketch(context, id + "F41", { "sketchPlane" : qUnion([Q0])});
            skCircle(sketch, "E52", {"center": v(-54.42, 4.77) * mm, "radius": 7.94 * mm});
            skCircle(sketch, "E53", {"center": v(-54.42, 4.77) * mm, "radius": 4.76 * mm});
            skSolve(sketch);
        }
        {
            var Q0;
            Q0=makeQuery(id+"F41.imprint","IMPRINT",FACE,{"disambiguationData":[TD([[makeQuery(id+"F41.imprint","IMPRINT",EDGE,{"derivedFrom":sQuery(id+"F41.wireOp",EDGE,"E52")}),1.0]])]});
            extrude(context, id + "F42", {"entities" : qUnion([Q0]), "oppositeDirection" : true, "depth" : 4.75 * mm});
        }
        {
            var Q0;
            Q0=makeQuery(id+"F15.opExtrude","CAP_FACE",FACE,{"disambiguationData":[OSD([sQuery(id+"F14.wireOp",EDGE,"E15.bottom"),sQuery(id+"F14.wireOp",EDGE,"E15.top"),sQuery(id+"F14.wireOp",EDGE,"E15.left"),sQuery(id+"F14.wireOp",EDGE,"E15.right"),sQuery(id+"F14.wireOp",EDGE,"E19"),sQuery(id+"F14.wireOp",EDGE,"E20")])],"isStart":true});
            cPlane(context, id + "F43", {"entities" : qUnion([Q0]), "cplaneType" : CPlaneType.OFFSET, "offset" : 25.4 * mm, "width" : 152.4 * mm, "height" : 152.4 * mm});
        }
        {
            var Q0;
            Q0=qCreatedBy(id+"F43.planeOp",FACE);
            var sketch = newSketch(context, id + "F44", { "sketchPlane" : qUnion([Q0])});
            skCircle(sketch, "E54.0", {"center": v(-117.64, -5.25) * mm, "radius": 1.9 * mm, "construction": true});
            skCircle(sketch, "E55.0", {"center": v(-117.64, -5.25) * mm, "radius": 4.76 * mm, "construction": true});
            skCircle(sketch, "E56.cCircle", {"center": v(-117.64, -5.25) * mm, "radius": 3.8 * mm, "construction": true});
            skLineSegment(sketch, "E56.0", {"start": v(-113.24, -5.25) * mm, "end": v(-115.44, -9.06) * mm});
            skLineSegment(sketch, "E56.1", {"start": v(-115.44, -9.06) * mm, "end": v(-119.84, -9.06) * mm});
            skLineSegment(sketch, "E56.2", {"start": v(-119.84, -9.06) * mm, "end": v(-122.04, -5.25) * mm});
            skLineSegment(sketch, "E56.3", {"start": v(-122.04, -5.25) * mm, "end": v(-119.84, -1.44) * mm});
            skLineSegment(sketch, "E56.4", {"start": v(-119.84, -1.44) * mm, "end": v(-115.44, -1.44) * mm});
            skLineSegment(sketch, "E56.5", {"start": v(-115.44, -1.44) * mm, "end": v(-113.24, -5.25) * mm});
            skPoint(sketch, "E56.0.midPoint", {"position": v(-114.34, -7.16) * mm});
            skCircle(sketch, "E57", {"center": v(-117.64, -5.25) * mm, "radius": 1.9 * mm});
            skSolve(sketch);
        }
        {
            var Q0;
            Q0=makeQuery(id+"F44.imprint","IMPRINT",FACE,{"disambiguationData":[TD([[makeQuery(id+"F44.imprint","IMPRINT",EDGE,{"derivedFrom":sQuery(id+"F44.wireOp",EDGE,"E56.0")}),-1.0]])]});
            extrude(context, id + "F45", {"entities" : qUnion([Q0]), "depth" : 15.88 * mm});
        }
        {
            var Q0;
            Q0=makeQuery(id+"F15.opExtrude","SWEPT_FACE",FACE,{"disambiguationData":[OSD([sQuery(id+"F14.wireOp",EDGE,"E15.top")])]});
            cPlane(context, id + "F46", {"entities" : qUnion([Q0]), "cplaneType" : CPlaneType.OFFSET, "offset" : 12.7 * mm, "width" : 152.4 * mm, "height" : 152.4 * mm});
        }
        {
            var Q0;
            Q0=qCreatedBy(id+"F46.planeOp",FACE);
            var sketch = newSketch(context, id + "F47", { "sketchPlane" : qUnion([Q0])});
            skCircle(sketch, "E58.0", {"center": v(9.53, -68.74) * mm, "radius": 4.76 * mm});
            skSolve(sketch);
        }
        {
            var Q0;
            Q0=makeQuery(id+"F47.imprint","IMPRINT",FACE,{"disambiguationData":[TD([[makeQuery(id+"F47.imprint","IMPRINT",EDGE,{"derivedFrom":sQuery(id+"F47.wireOp",EDGE,"E58.0")}),1.0]])]});
            extrude(context, id + "F48", {"entities" : qUnion([Q0]), "depth" : 50.8 * mm});
        }
        {
            var Q0;
            Q0=qCreatedBy(id+"F46.planeOp",FACE);
            var sketch = newSketch(context, id + "F49", { "sketchPlane" : qUnion([Q0])});
            skCircle(sketch, "E59.cCircle", {"center": v(9.53, -113.2) * mm, "radius": 7.94 * mm, "construction": true});
            skLineSegment(sketch, "E59.0", {"start": v(18.7, -113.2) * mm, "end": v(14.1, -121.13) * mm});
            skLineSegment(sketch, "E59.1", {"start": v(14.1, -121.13) * mm, "end": v(4.94, -121.13) * mm});
            skLineSegment(sketch, "E59.2", {"start": v(4.94, -121.13) * mm, "end": v(0.36, -113.2) * mm});
            skLineSegment(sketch, "E59.3", {"start": v(0.36, -113.2) * mm, "end": v(4.94, -105.26) * mm});
            skLineSegment(sketch, "E59.4", {"start": v(4.94, -105.26) * mm, "end": v(14.1, -105.26) * mm});
            skLineSegment(sketch, "E59.5", {"start": v(14.1, -105.26) * mm, "end": v(18.7, -113.2) * mm});
            skPoint(sketch, "E59.0.midPoint", {"position": v(16.4, -117.16) * mm});
            skCircle(sketch, "E60.0", {"center": v(9.53, -113.2) * mm, "radius": 4.76 * mm});
            skSolve(sketch);
        }
        {
            var Q0;
            Q0=makeQuery(id+"F49.imprint","IMPRINT",FACE,{"disambiguationData":[TD([[makeQuery(id+"F49.imprint","IMPRINT",EDGE,{"derivedFrom":sQuery(id+"F49.wireOp",EDGE,"E59.0")}),-1.0]])]});
            extrude(context, id + "F50", {"entities" : qUnion([Q0]), "depth" : 4.75 * mm});
        }
        {
            var Q0;
            Q0=makeQuery(id+"F50.opExtrude","CAP_EDGE",EDGE,{"disambiguationData":[OSD([sQuery(id+"F49.wireOp",EDGE,"E59.2")])],"isStart":false});
            var Q1;
            Q1=makeQuery(id+"F50.opExtrude","CAP_EDGE",EDGE,{"disambiguationData":[OSD([sQuery(id+"F49.wireOp",EDGE,"E59.3")])],"isStart":false});
            var Q2;
            Q2=makeQuery(id+"F50.opExtrude","CAP_EDGE",EDGE,{"disambiguationData":[OSD([sQuery(id+"F49.wireOp",EDGE,"E59.4")])],"isStart":false});
            var Q3;
            Q3=makeQuery(id+"F50.opExtrude","CAP_EDGE",EDGE,{"disambiguationData":[OSD([sQuery(id+"F49.wireOp",EDGE,"E59.5")])],"isStart":false});
            var Q4;
            Q4=makeQuery(id+"F50.opExtrude","CAP_EDGE",EDGE,{"disambiguationData":[OSD([sQuery(id+"F49.wireOp",EDGE,"E59.0")])],"isStart":false});
            var Q5;
            Q5=makeQuery(id+"F50.opExtrude","CAP_EDGE",EDGE,{"disambiguationData":[OSD([sQuery(id+"F49.wireOp",EDGE,"E59.1")])],"isStart":false});
            var Q6;
            Q6=makeQuery(id+"F50.opExtrude","CAP_EDGE",EDGE,{"disambiguationData":[OSD([sQuery(id+"F49.wireOp",EDGE,"E59.2")])],"isStart":true});
            var Q7;
            Q7=makeQuery(id+"F50.opExtrude","CAP_EDGE",EDGE,{"disambiguationData":[OSD([sQuery(id+"F49.wireOp",EDGE,"E59.1")])],"isStart":true});
            var Q8;
            Q8=makeQuery(id+"F50.opExtrude","CAP_EDGE",EDGE,{"disambiguationData":[OSD([sQuery(id+"F49.wireOp",EDGE,"E59.0")])],"isStart":true});
            var Q9;
            Q9=makeQuery(id+"F50.opExtrude","CAP_EDGE",EDGE,{"disambiguationData":[OSD([sQuery(id+"F49.wireOp",EDGE,"E59.5")])],"isStart":true});
            var Q10;
            Q10=makeQuery(id+"F50.opExtrude","CAP_EDGE",EDGE,{"disambiguationData":[OSD([sQuery(id+"F49.wireOp",EDGE,"E59.4")])],"isStart":true});
            var Q11;
            Q11=makeQuery(id+"F50.opExtrude","CAP_EDGE",EDGE,{"disambiguationData":[OSD([sQuery(id+"F49.wireOp",EDGE,"E59.3")])],"isStart":true});
            fillet(context, id + "F51", {"entities" : qUnion([Q0, Q1, Q2, Q3, Q4, Q5, Q6, Q7, Q8, Q9, Q10, Q11]), "radius" : 0.5 * mm, "tangentPropagation" : true, "allowEdgeOverflow" : false});
        }
    });
